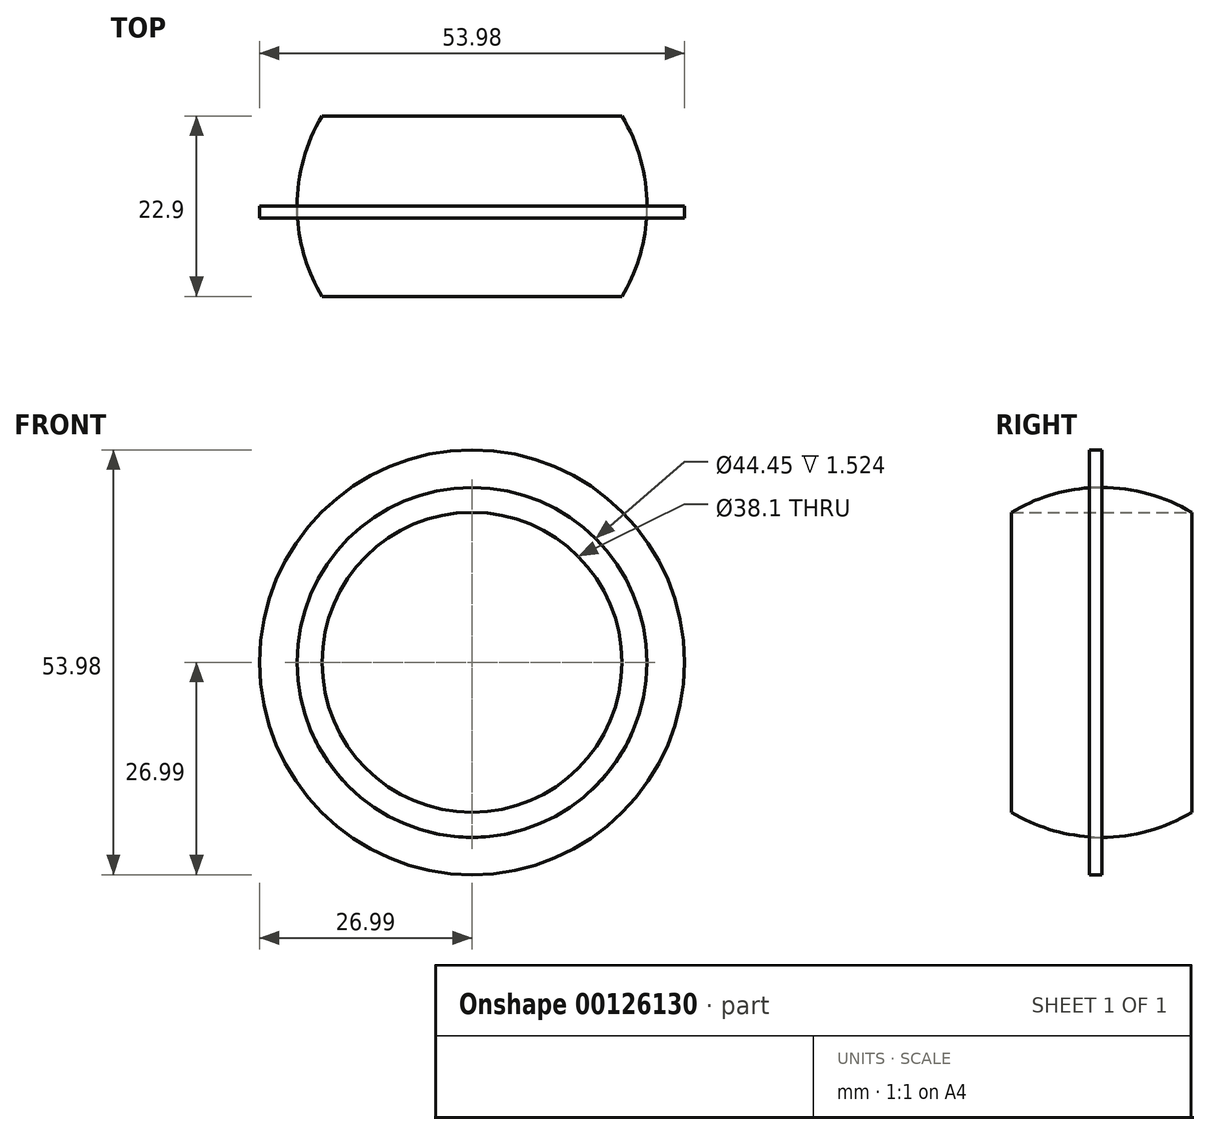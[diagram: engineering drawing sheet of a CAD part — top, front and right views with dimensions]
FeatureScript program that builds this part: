
annotation { "Feature Type Name" : "Feature", "Feature Type Description" : "" }
export const myFeature = defineFeature(function(context is Context, id is Id, definition is map)
    precondition{}
    {
        {
            var Q0;
            Q0=qCreatedBy(makeId("Front.planeOp"),FACE);
            var sketch = newSketch(context, id + "F0", { "sketchPlane" : qUnion([Q0])});
            skCircle(sketch, "E0", {"center": v(0, 0) * mm, "radius": 26.99 * mm});
            skCircle(sketch, "E1", {"center": v(0, 0) * mm, "radius": 22.23 * mm});
            skLineSegment(sketch, "E2", {"start": v(-55.5, 0) * mm, "end": v(54.64, 0) * mm});
            skLineSegment(sketch, "E3", {"start": v(0, 41.12) * mm, "end": v(0, -44.26) * mm});
            skCircle(sketch, "E4", {"center": v(0, 0) * mm, "radius": 19.05 * mm});
            skSolve(sketch);
        }
        {
            var Q0;
            {var subQ0=sQuery(id+"F0.wireOp",EDGE,"E3");var subQ1=sQuery(id+"F0.wireOp",EDGE,"E1");var subQ2=makeQuery(id+"F0.imprint","INTERSECT",VERTEX,{"disambiguationData":[OD(0.0)],"derivedFrom":[subQ1,subQ0]});Q0=makeQuery(id+"F0.imprint","IMPRINT",FACE,{"disambiguationData":[TD([[makeQuery(id+"F0.imprint","IMPRINT",EDGE,{"disambiguationData":[TD([[subQ2,-1.0]])],"derivedFrom":subQ1}),1.0]])]});}
            var Q1;
            {var subQ0=sQuery(id+"F0.wireOp",EDGE,"E3");var subQ1=sQuery(id+"F0.wireOp",EDGE,"E1");var subQ2=makeQuery(id+"F0.imprint","INTERSECT",VERTEX,{"disambiguationData":[OD(0.0)],"derivedFrom":[subQ1,subQ0]});Q1=makeQuery(id+"F0.imprint","IMPRINT",FACE,{"disambiguationData":[TD([[makeQuery(id+"F0.imprint","IMPRINT",EDGE,{"disambiguationData":[TD([[subQ2,1.0]])],"derivedFrom":subQ1}),1.0]])]});}
            var Q2;
            Q2=sQuery(id+"F0.wireOp",EDGE,"E2");
            revolve(context, id + "F1", {"entities" : qUnion([Q0, Q1]), "axis" : qUnion([Q2]), "revolveType" : RevolveType.SYMMETRIC, "angle" : 360 * degree});
        }
        {
            var Q0;
            {var subQ0=sQuery(id+"F0.wireOp",EDGE,"E3");var subQ1=sQuery(id+"F0.wireOp",EDGE,"E0");var subQ2=makeQuery(id+"F0.imprint","INTERSECT",VERTEX,{"disambiguationData":[OD(0.0)],"derivedFrom":[subQ1,subQ0]});Q0=makeQuery(id+"F0.imprint","IMPRINT",FACE,{"disambiguationData":[TD([[makeQuery(id+"F0.imprint","IMPRINT",EDGE,{"disambiguationData":[TD([[subQ2,-1.0]])],"derivedFrom":subQ1}),1.0]])]});}
            var Q1;
            {var subQ0=sQuery(id+"F0.wireOp",EDGE,"E3");var subQ1=sQuery(id+"F0.wireOp",EDGE,"E0");var subQ2=makeQuery(id+"F0.imprint","INTERSECT",VERTEX,{"disambiguationData":[OD(0.0)],"derivedFrom":[subQ1,subQ0]});Q1=makeQuery(id+"F0.imprint","IMPRINT",FACE,{"disambiguationData":[TD([[makeQuery(id+"F0.imprint","IMPRINT",EDGE,{"disambiguationData":[TD([[subQ2,1.0]])],"derivedFrom":subQ1}),1.0]])]});}
            var Q2;
            {var subQ0=sQuery(id+"F0.wireOp",EDGE,"E2");var subQ1=sQuery(id+"F0.wireOp",EDGE,"E0");var subQ2=makeQuery(id+"F0.imprint","INTERSECT",VERTEX,{"disambiguationData":[OD(0.0)],"derivedFrom":[subQ1,subQ0]});Q2=makeQuery(id+"F0.imprint","IMPRINT",FACE,{"disambiguationData":[TD([[makeQuery(id+"F0.imprint","IMPRINT",EDGE,{"disambiguationData":[TD([[subQ2,1.0]])],"derivedFrom":subQ1}),1.0]])]});}
            var Q3;
            {var subQ0=sQuery(id+"F0.wireOp",EDGE,"E2");var subQ1=sQuery(id+"F0.wireOp",EDGE,"E0");var subQ2=makeQuery(id+"F0.imprint","INTERSECT",VERTEX,{"disambiguationData":[OD(1.0)],"derivedFrom":[subQ1,subQ0]});Q3=makeQuery(id+"F0.imprint","IMPRINT",FACE,{"disambiguationData":[TD([[makeQuery(id+"F0.imprint","IMPRINT",EDGE,{"disambiguationData":[TD([[subQ2,-1.0]])],"derivedFrom":subQ1}),1.0]])]});}
            extrude(context, id + "F2", {"entities" : qUnion([Q0, Q1, Q2, Q3]), "depth" : 1.52 * mm});
        }
        {
            var Q0;
            {var subQ0=sQuery(id+"F0.wireOp",EDGE,"E3");var subQ1=sQuery(id+"F0.wireOp",EDGE,"E2");var subQ2=makeQuery(id+"F0.imprint","INTERSECT",VERTEX,{"derivedFrom":[subQ1,subQ0]});Q0=makeQuery(id+"F0.imprint","IMPRINT",FACE,{"disambiguationData":[TD([[makeQuery(id+"F0.imprint","IMPRINT",EDGE,{"disambiguationData":[TD([[subQ2,-1.0]])],"derivedFrom":subQ1}),-1.0]])]});}
            var Q1;
            {var subQ0=sQuery(id+"F0.wireOp",EDGE,"E4");var subQ1=sQuery(id+"F0.wireOp",EDGE,"E2");var subQ2=makeQuery(id+"F0.imprint","INTERSECT",VERTEX,{"disambiguationData":[OD(0.0)],"derivedFrom":[subQ1,subQ0]});Q1=makeQuery(id+"F0.imprint","IMPRINT",FACE,{"disambiguationData":[TD([[makeQuery(id+"F0.imprint","IMPRINT",EDGE,{"disambiguationData":[TD([[subQ2,-1.0]])],"derivedFrom":subQ1}),-1.0]])]});}
            var Q2;
            {var subQ0=sQuery(id+"F0.wireOp",EDGE,"E4");var subQ1=sQuery(id+"F0.wireOp",EDGE,"E2");var subQ2=makeQuery(id+"F0.imprint","INTERSECT",VERTEX,{"disambiguationData":[OD(0.0)],"derivedFrom":[subQ1,subQ0]});Q2=makeQuery(id+"F0.imprint","IMPRINT",FACE,{"disambiguationData":[TD([[makeQuery(id+"F0.imprint","IMPRINT",EDGE,{"disambiguationData":[TD([[subQ2,-1.0]])],"derivedFrom":subQ1}),1.0]])]});}
            var Q3;
            {var subQ0=sQuery(id+"F0.wireOp",EDGE,"E3");var subQ1=sQuery(id+"F0.wireOp",EDGE,"E2");var subQ2=makeQuery(id+"F0.imprint","INTERSECT",VERTEX,{"derivedFrom":[subQ1,subQ0]});Q3=makeQuery(id+"F0.imprint","IMPRINT",FACE,{"disambiguationData":[TD([[makeQuery(id+"F0.imprint","IMPRINT",EDGE,{"disambiguationData":[TD([[subQ2,-1.0]])],"derivedFrom":subQ1}),1.0]])]});}
            extrude(context, id + "F3", {"entities" : qUnion([Q0, Q1, Q2, Q3]), "operationType" : NewBodyOperationType.REMOVE, "depth" : 113.03 * mm, "symmetric" : true});
        }
    });
